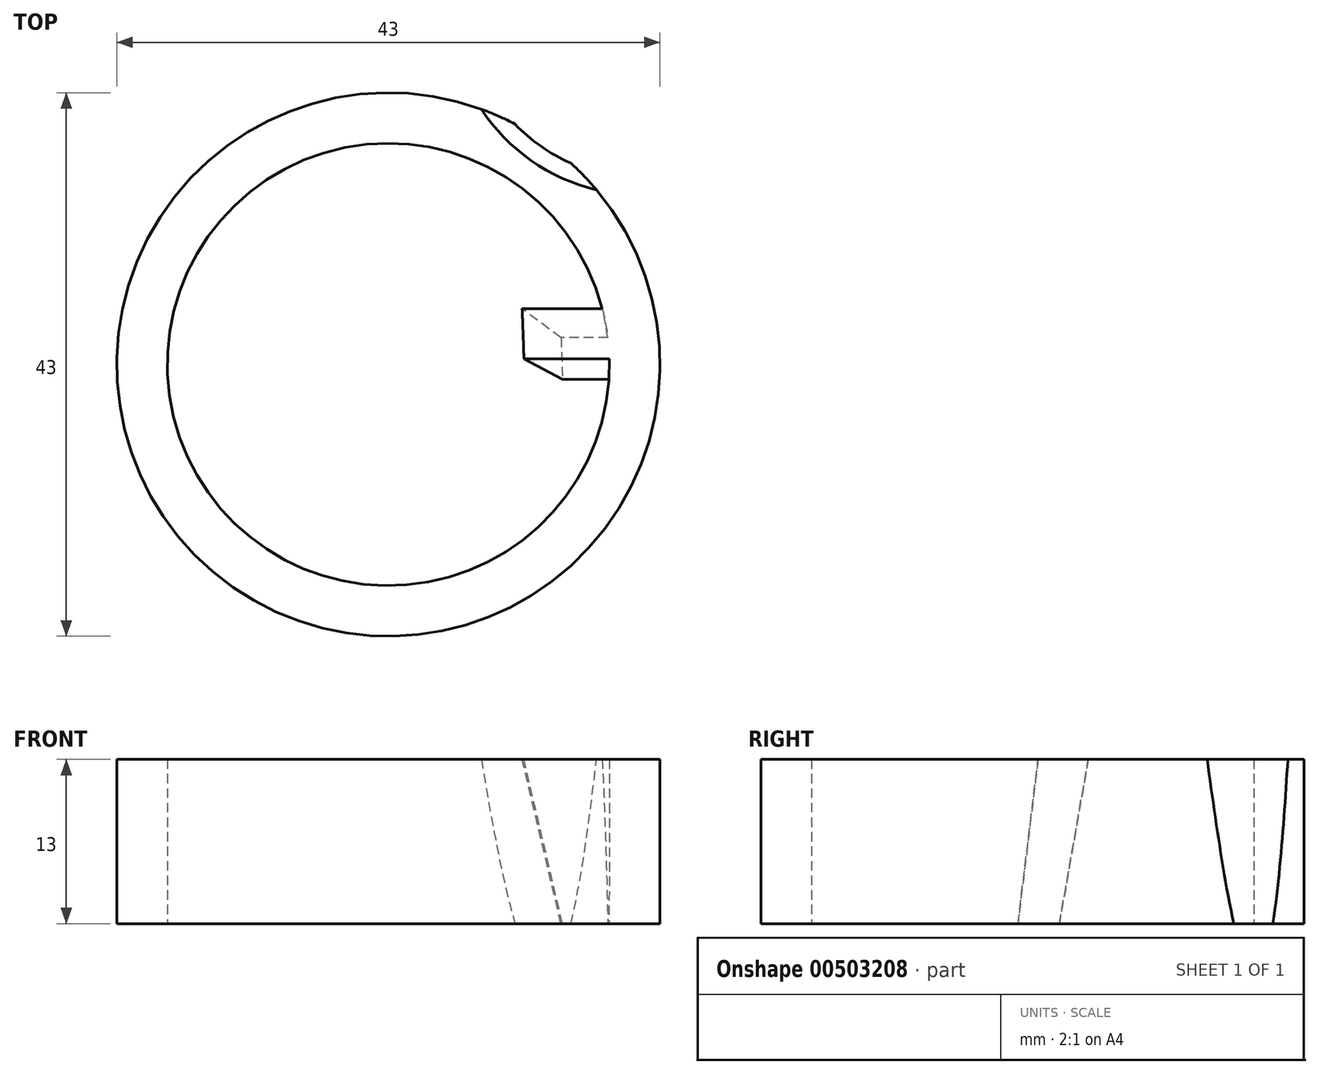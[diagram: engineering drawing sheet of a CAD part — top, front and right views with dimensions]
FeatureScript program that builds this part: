
annotation { "Feature Type Name" : "Feature", "Feature Type Description" : "" }
export const myFeature = defineFeature(function(context is Context, id is Id, definition is map)
    precondition{}
    {
        {
            var Q0;
            Q0=qCreatedBy(makeId("Top.planeOp"),FACE);
            var sketch = newSketch(context, id + "F0", { "sketchPlane" : qUnion([Q0])});
            skCircle(sketch, "E0", {"center": v(0, 0) * mm, "radius": 21.5 * mm});
            skCircle(sketch, "E1", {"center": v(0, 0) * mm, "radius": 17.5 * mm});
            skSolve(sketch);
        }
        {
            var Q0;
            Q0 = qSketchRegion(id + "F0", true);
            extrude(context, id + "F1", {"entities" : qUnion([Q0]), "depth" : 25 * mm});
        }
        {
            var Q0;
            Q0=qCreatedBy(makeId("Front.planeOp"),FACE);
            var sketch = newSketch(context, id + "F2", { "sketchPlane" : qUnion([Q0])});
            skLineSegment(sketch, "E2", {"start": v(0, 0) * mm, "end": v(0, 25) * mm, "construction": true});
            skLineSegment(sketch, "E3", {"start": v(0, 0) * mm, "end": v(21.18, 0) * mm, "construction": true});
            skSolve(sketch);
        }
        {
            var Q0;
            Q0=sQuery(id+"F2.wireOp",EDGE,"E3");
            cPlane(context, id + "F3", {"entities" : qUnion([Q0]), "cplaneType" : CPlaneType.LINE_ANGLE, "offset" : 25 * mm, "angle" : 10 * degree, "oppositeDirection" : true, "width" : 150 * mm, "height" : 150 * mm});
        }
        {
            var Q0;
            Q0=qCreatedBy(id+"F3.planeOp",FACE);
            var sketch = newSketch(context, id + "F4", { "sketchPlane" : qUnion([Q0])});
            skLineSegment(sketch, "E4", {"start": v(-17.5, 0) * mm, "end": v(-16.5, 0) * mm, "construction": true});
            skLineSegment(sketch, "E5", {"start": v(-16.73, -1) * mm, "end": v(-9.5, 30.06) * mm});
            skLineSegment(sketch, "E6", {"start": v(-9.5, 30.06) * mm, "end": v(-17.5, 30.06) * mm});
            skLineSegment(sketch, "E7", {"start": v(-17.5, 30.06) * mm, "end": v(-17.5, -1) * mm});
            skLineSegment(sketch, "E8", {"start": v(0, -50) * mm, "end": v(-21.5, -50) * mm, "construction": true});
            skLineSegment(sketch, "E9", {"start": v(-17.5, -1) * mm, "end": v(-16.73, -1) * mm});
            skSolve(sketch);
        }
        {
            var Q0;
            Q0 = qSketchRegion(id + "F4", true);
            var Q1;
            Q1=sQuery(id+"F4.wireOp",EDGE,"E8");
            revolve(context, id + "F5", {"operationType" : NewBodyOperationType.ADD, "entities" : qUnion([Q0]), "axis" : qUnion([Q1]), "revolveType" : RevolveType.ONE_DIRECTION, "angle" : 3 * degree});
        }
        {
            var Q0;
            Q0=makeQuery(id+"F9.boolean.opBoolean","MERGE",FACE,{"derivedFrom":[makeQuery(id+"F1.opExtrude","CAP_FACE",FACE,{"disambiguationData":[OSD([sQuery(id+"F0.wireOp",EDGE,"E0"),sQuery(id+"F0.wireOp",EDGE,"E1")])],"isStart":false}),makeQuery(id+"F9.opExtrude","SWEPT_FACE",FACE,{"disambiguationData":[OSD([sQuery(id+"F8.wireOp",EDGE,"E15")])]})]});
            var sketch = newSketch(context, id + "F6", { "sketchPlane" : qUnion([Q0])});
            skArc(sketch, "E10", {"start": v(7.35, 20.2) * mm, "mid": v(11.3, 16.13) * mm, "end": v(16.47, 13.82) * mm});
            skLineSegment(sketch, "E11", {"start": v(7.35, 20.2) * mm, "end": v(0, 0) * mm, "construction": true});
            skLineSegment(sketch, "E12", {"start": v(0, 0) * mm, "end": v(16.47, 13.82) * mm, "construction": true});
            skLineSegment(sketch, "E13", {"start": v(0, 0) * mm, "end": v(27.32, 0) * mm, "construction": true});
            skArc(sketch, "E14", {"start": v(16.47, 13.82) * mm, "mid": v(13.74, 19.62) * mm, "end": v(7.35, 20.2) * mm});
            skSolve(sketch);
        }
        {
            var Q0;
            Q0 = qSketchRegion(id + "F6", true);
            extrude(context, id + "F7", {"entities" : qUnion([Q0]), "operationType" : NewBodyOperationType.REMOVE, "oppositeDirection" : true, "depth" : 30 * mm, "hasDraft" : true, "draftAngle" : 6 * degree, "draftPullDirection" : true});
        }
        {
            var Q0;
            Q0=qCreatedBy(makeId("Front.planeOp"),FACE);
            var sketch = newSketch(context, id + "F8", { "sketchPlane" : qUnion([Q0])});
            skLineSegment(sketch, "E15", {"start": v(-64.84, 25) * mm, "end": v(90.2, 25) * mm});
            skLineSegment(sketch, "E16", {"start": v(90.2, 25) * mm, "end": v(90.2, 12) * mm});
            skLineSegment(sketch, "E17", {"start": v(90.2, 12) * mm, "end": v(-68.08, 12) * mm});
            skLineSegment(sketch, "E18", {"start": v(-68.08, 12) * mm, "end": v(-68.08, -12.3) * mm});
            skLineSegment(sketch, "E19", {"start": v(-68.08, -12.3) * mm, "end": v(119.68, -12.3) * mm});
            skLineSegment(sketch, "E20", {"start": v(119.68, -12.3) * mm, "end": v(119.68, 47) * mm});
            skLineSegment(sketch, "E21", {"start": v(119.68, 47) * mm, "end": v(-64.84, 47) * mm});
            skLineSegment(sketch, "E22", {"start": v(-64.84, 47) * mm, "end": v(-64.84, 25) * mm});
            skSolve(sketch);
        }
        {
            var Q0;
            Q0 = qSketchRegion(id + "F8", true);
            extrude(context, id + "F9", {"entities" : qUnion([Q0]), "operationType" : NewBodyOperationType.REMOVE, "endBound" : BoundingType.SYMMETRIC, "depth" : 60 * mm});
        }
    });
